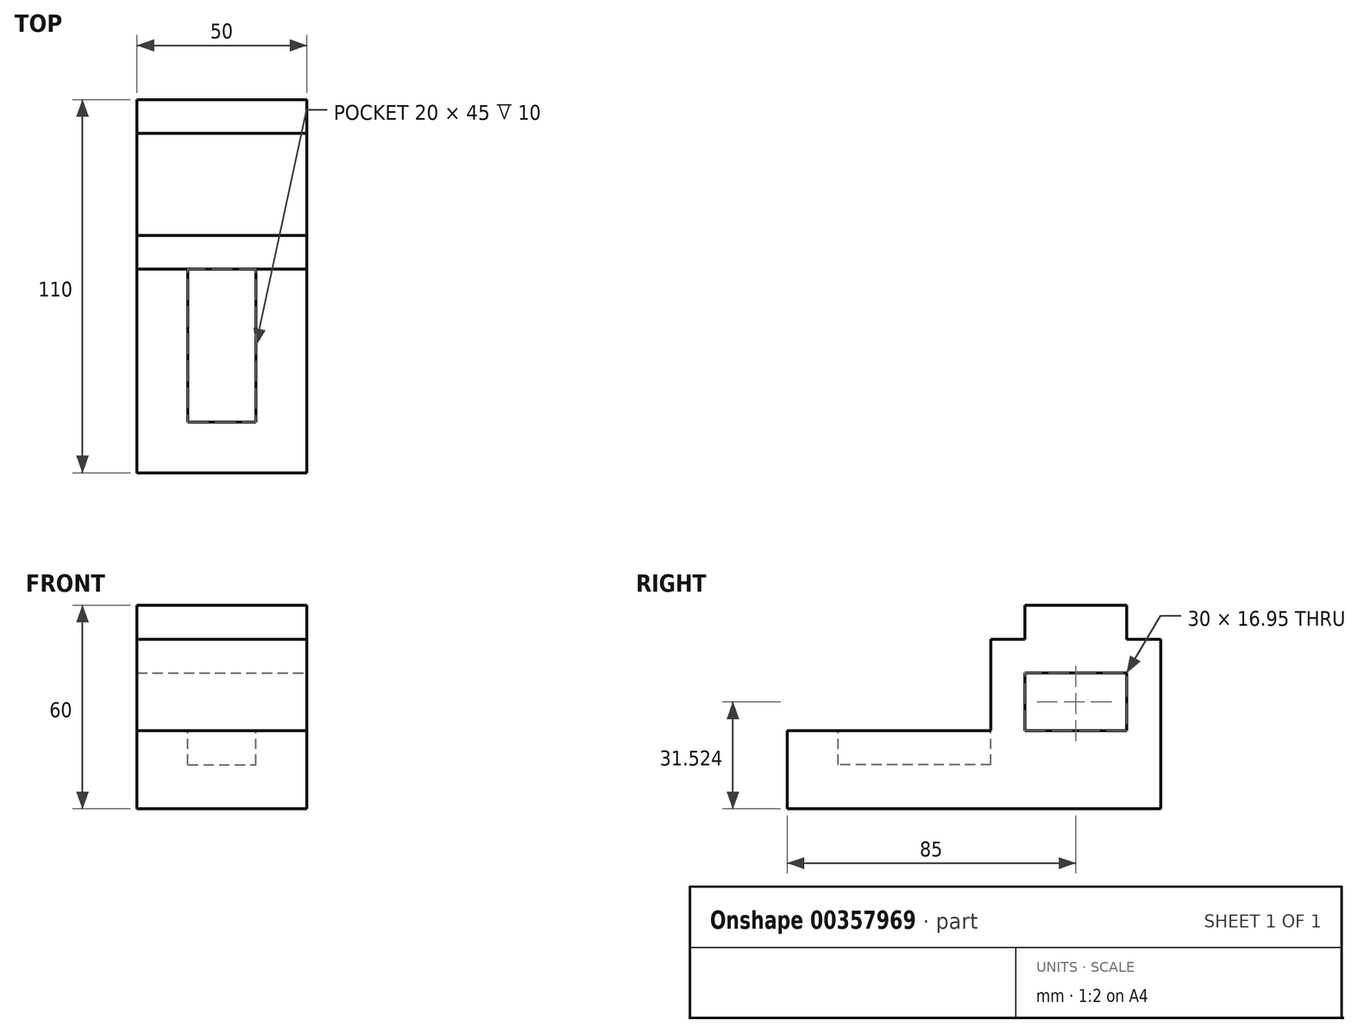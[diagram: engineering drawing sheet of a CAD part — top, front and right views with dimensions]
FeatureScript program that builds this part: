
annotation { "Feature Type Name" : "Feature", "Feature Type Description" : "" }
export const myFeature = defineFeature(function(context is Context, id is Id, definition is map)
    precondition{}
    {
        {
            var Q0;
            Q0=qCreatedBy(makeId("Top.planeOp"),FACE);
            var sketch = newSketch(context, id + "F0", { "sketchPlane" : qUnion([Q0])});
            skLineSegment(sketch, "E0.bottom", {"start": v(-25, 55) * mm, "end": v(25, 55) * mm});
            skLineSegment(sketch, "E0.top", {"start": v(-25, -55) * mm, "end": v(25, -55) * mm});
            skLineSegment(sketch, "E0.left", {"start": v(-25, 55) * mm, "end": v(-25, -55) * mm});
            skLineSegment(sketch, "E0.right", {"start": v(25, 55) * mm, "end": v(25, -55) * mm});
            skPoint(sketch, "E0.middle", {"position": v(0, 0) * mm});
            skSolve(sketch);
        }
        {
            var Q0;
            Q0 = qSketchRegion(id + "F0", true);
            extrude(context, id + "F1", {"entities" : qUnion([Q0]), "depth" : 60 * mm});
        }
        {
            var Q0;
            Q0=makeQuery(id+"F1.opExtrude","SWEPT_FACE",FACE,{"disambiguationData":[OSD([sQuery(id+"F0.wireOp",EDGE,"E0.right")])]});
            var sketch = newSketch(context, id + "F2", { "sketchPlane" : qUnion([Q0])});
            skLineSegment(sketch, "E1.bottom", {"start": v(15, 40) * mm, "end": v(45, 40) * mm});
            skLineSegment(sketch, "E1.top", {"start": v(15, 23.05) * mm, "end": v(45, 23.05) * mm});
            skLineSegment(sketch, "E1.left", {"start": v(15, 40) * mm, "end": v(15, 23.05) * mm});
            skLineSegment(sketch, "E1.right", {"start": v(45, 40) * mm, "end": v(45, 23.05) * mm});
            skPoint(sketch, "E1.middle", {"position": v(30, 31.52) * mm});
            skLineSegment(sketch, "E2.bottom", {"start": v(55, 60) * mm, "end": v(45, 60) * mm});
            skLineSegment(sketch, "E2.top", {"start": v(55, 50) * mm, "end": v(45, 50) * mm});
            skLineSegment(sketch, "E2.left", {"start": v(55, 60) * mm, "end": v(55, 50) * mm});
            skLineSegment(sketch, "E2.right", {"start": v(45, 60) * mm, "end": v(45, 50) * mm});
            skLineSegment(sketch, "E3.bottom", {"start": v(15, 60) * mm, "end": v(5, 60) * mm});
            skLineSegment(sketch, "E3.top", {"start": v(15, 50) * mm, "end": v(5, 50) * mm});
            skLineSegment(sketch, "E3.left", {"start": v(15, 60) * mm, "end": v(15, 50) * mm});
            skLineSegment(sketch, "E3.right", {"start": v(5, 60) * mm, "end": v(5, 50) * mm});
            skLineSegment(sketch, "E4.bottom", {"start": v(-55, 60) * mm, "end": v(5, 60) * mm});
            skLineSegment(sketch, "E4.top", {"start": v(-55, 23.05) * mm, "end": v(5, 23.05) * mm});
            skLineSegment(sketch, "E4.left", {"start": v(-55, 60) * mm, "end": v(-55, 23.05) * mm});
            skLineSegment(sketch, "E4.right", {"start": v(5, 60) * mm, "end": v(5, 23.05) * mm});
            skSolve(sketch);
        }
        {
            var Q0;
            Q0 = qSketchRegion(id + "F2", true);
            extrude(context, id + "F3", {"entities" : qUnion([Q0]), "operationType" : NewBodyOperationType.REMOVE, "endBound" : BoundingType.THROUGH_ALL, "oppositeDirection" : true, "depth" : 25 * mm});
        }
        {
            var Q0;
            Q0=makeQuery(id+"F3.boolean.opBoolean","COPY",FACE,{"derivedFrom":makeQuery(id+"F3.opExtrude","SWEPT_FACE",FACE,{"disambiguationData":[OSD([sQuery(id+"F2.wireOp",EDGE,"E4.top")])]})});
            var sketch = newSketch(context, id + "F4", { "sketchPlane" : qUnion([Q0])});
            skLineSegment(sketch, "E5.bottom", {"start": v(-10, 5) * mm, "end": v(10, 5) * mm});
            skLineSegment(sketch, "E5.top", {"start": v(-10, -40) * mm, "end": v(10, -40) * mm});
            skLineSegment(sketch, "E5.left", {"start": v(-10, 5) * mm, "end": v(-10, -40) * mm});
            skLineSegment(sketch, "E5.right", {"start": v(10, 5) * mm, "end": v(10, -40) * mm});
            skSolve(sketch);
        }
        {
            var Q0;
            Q0 = qSketchRegion(id + "F4", true);
            extrude(context, id + "F5", {"entities" : qUnion([Q0]), "operationType" : NewBodyOperationType.REMOVE, "oppositeDirection" : true, "depth" : 10 * mm});
        }
    });
